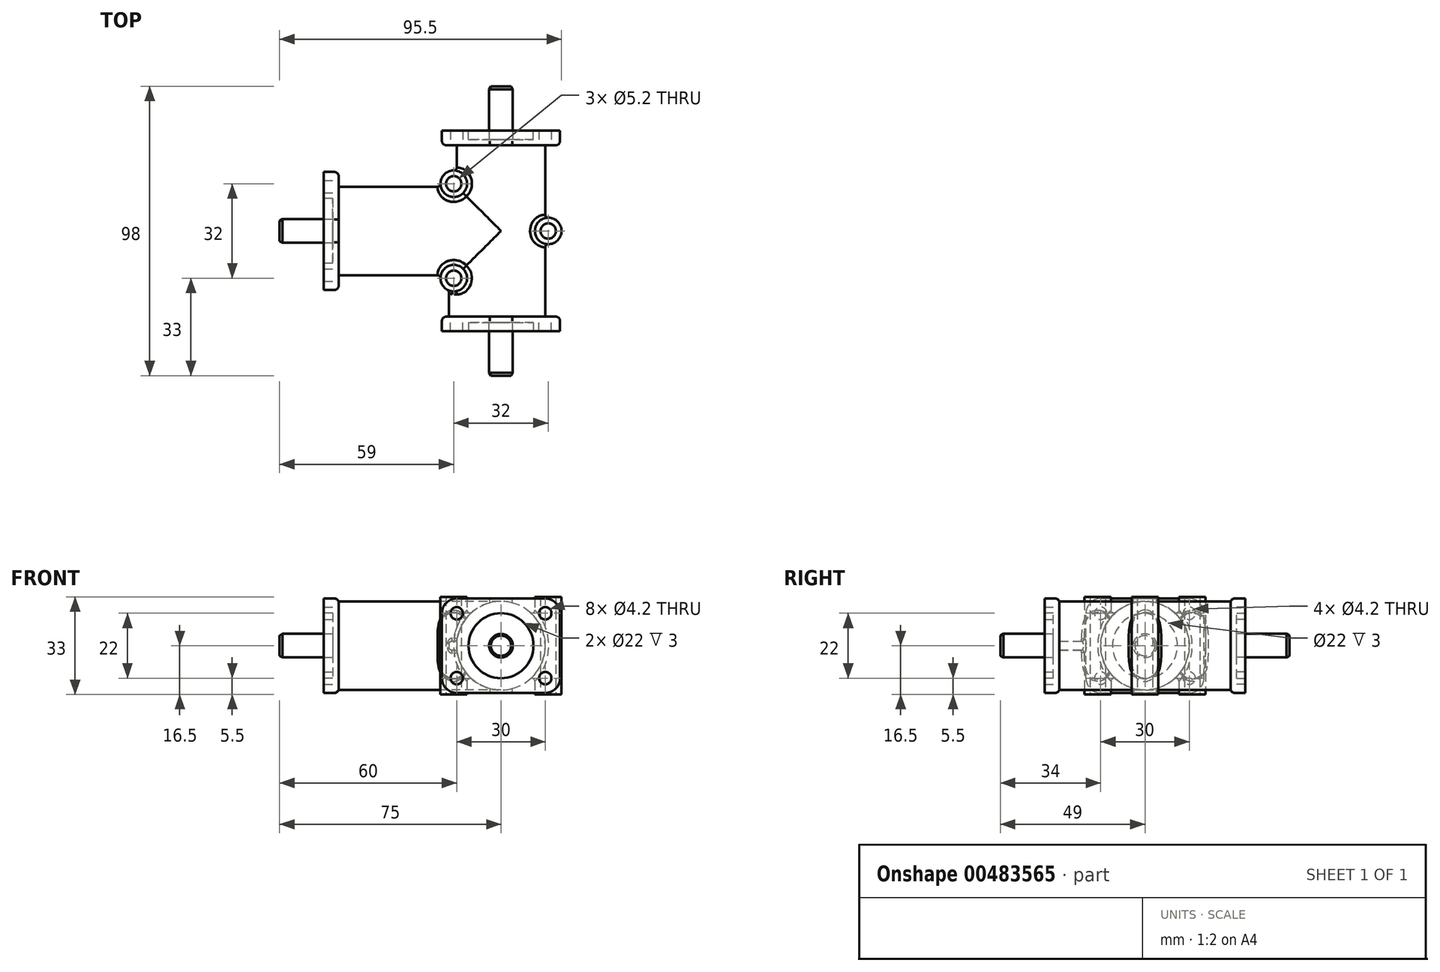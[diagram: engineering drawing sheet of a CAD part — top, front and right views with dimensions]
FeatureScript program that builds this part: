
annotation { "Feature Type Name" : "Feature", "Feature Type Description" : "" }
export const myFeature = defineFeature(function(context is Context, id is Id, definition is map)
    precondition{}
    {
        {
            var Q0;
            Q0=qCreatedBy(makeId("Right.planeOp"),FACE);
            var sketch = newSketch(context, id + "F0", { "sketchPlane" : qUnion([Q0])});
            skCircle(sketch, "E0", {"center": v(0, 0) * mm, "radius": 15 * mm});
            skSolve(sketch);
        }
        {
            var Q0;
            Q0 = qSketchRegion(id + "F0", true);
            extrude(context, id + "F1", {"entities" : qUnion([Q0]), "depth" : 55 * mm});
        }
        {
            var Q0;
            Q0=qCreatedBy(makeId("Front.planeOp"),FACE);
            var sketch = newSketch(context, id + "F2", { "sketchPlane" : qUnion([Q0])});
            skCircle(sketch, "E1", {"center": v(55, 0) * mm, "radius": 15 * mm});
            skSolve(sketch);
        }
        {
            var Q0;
            Q0 = qSketchRegion(id + "F2", true);
            extrude(context, id + "F3", {"entities" : qUnion([Q0]), "operationType" : NewBodyOperationType.ADD, "endBound" : BoundingType.SYMMETRIC, "depth" : 58 * mm});
        }
        {
            var Q0;
            Q0=qCreatedBy(makeId("Top.planeOp"),FACE);
            var sketch = newSketch(context, id + "F4", { "sketchPlane" : qUnion([Q0])});
            skCircle(sketch, "E2", {"center": v(39, 16) * mm, "radius": 4.5 * mm});
            skCircle(sketch, "E3", {"center": v(39, -16) * mm, "radius": 4.5 * mm});
            skLineSegment(sketch, "E4", {"start": v(0, 0) * mm, "end": v(71, 0) * mm, "construction": true});
            skCircle(sketch, "E5", {"center": v(71, 0) * mm, "radius": 4.5 * mm});
            skCircle(sketch, "E6", {"center": v(39, 16) * mm, "radius": 2.75 * mm});
            skCircle(sketch, "E7", {"center": v(39, -16) * mm, "radius": 2.75 * mm});
            skCircle(sketch, "E8", {"center": v(71, 0) * mm, "radius": 2.75 * mm});
            skSolve(sketch);
        }
        {
            var Q0;
            Q0=makeQuery(id+"F4.imprint","IMPRINT",FACE,{"disambiguationData":[TD([[makeQuery(id+"F4.imprint","IMPRINT",EDGE,{"derivedFrom":sQuery(id+"F4.wireOp",EDGE,"E7")}),1.0]])]});
            var Q1;
            Q1=makeQuery(id+"F4.imprint","IMPRINT",FACE,{"disambiguationData":[TD([[makeQuery(id+"F4.imprint","IMPRINT",EDGE,{"derivedFrom":sQuery(id+"F4.wireOp",EDGE,"E6")}),1.0]])]});
            var Q2;
            Q2=makeQuery(id+"F4.imprint","IMPRINT",FACE,{"disambiguationData":[TD([[makeQuery(id+"F4.imprint","IMPRINT",EDGE,{"derivedFrom":sQuery(id+"F4.wireOp",EDGE,"E8")}),1.0]])]});
            var Q3;
            Q3=makeQuery(id+"F4.imprint","IMPRINT",FACE,{"disambiguationData":[TD([[makeQuery(id+"F4.imprint","IMPRINT",EDGE,{"derivedFrom":sQuery(id+"F4.wireOp",EDGE,"E3")}),1.0]])]});
            var Q4;
            Q4=makeQuery(id+"F4.imprint","IMPRINT",FACE,{"disambiguationData":[TD([[makeQuery(id+"F4.imprint","IMPRINT",EDGE,{"derivedFrom":sQuery(id+"F4.wireOp",EDGE,"E5")}),1.0]])]});
            var Q5;
            Q5=makeQuery(id+"F4.imprint","IMPRINT",FACE,{"disambiguationData":[TD([[makeQuery(id+"F4.imprint","IMPRINT",EDGE,{"derivedFrom":sQuery(id+"F4.wireOp",EDGE,"E2")}),1.0]])]});
            extrude(context, id + "F5", {"entities" : qUnion([Q0, Q1, Q2, Q3, Q4, Q5]), "operationType" : NewBodyOperationType.ADD, "endBound" : BoundingType.SYMMETRIC, "depth" : 33 * mm});
        }
        {
            var Q0;
            Q0=qCreatedBy(makeId("Top.planeOp"),FACE);
            var sketch = newSketch(context, id + "F6", { "sketchPlane" : qUnion([Q0])});
            skCircle(sketch, "E9", {"center": v(39, -16) * mm, "radius": 2.6 * mm});
            skCircle(sketch, "E10", {"center": v(39, 16) * mm, "radius": 2.6 * mm});
            skCircle(sketch, "E11", {"center": v(71, 0) * mm, "radius": 2.6 * mm});
            skSolve(sketch);
        }
        {
            var Q0;
            Q0 = qSketchRegion(id + "F6", true);
            extrude(context, id + "F7", {"entities" : qUnion([Q0]), "operationType" : NewBodyOperationType.REMOVE, "endBound" : BoundingType.SYMMETRIC, "depth" : 33 * mm});
        }
        {
            var Q0;
            Q0=makeQuery(id+"F1.opExtrude","CAP_FACE",FACE,{"disambiguationData":[OSD([sQuery(id+"F0.wireOp",EDGE,"E0")])],"isStart":true});
            var sketch = newSketch(context, id + "F8", { "sketchPlane" : qUnion([Q0])});
            skLineSegment(sketch, "E12.bottom", {"start": v(15, -16) * mm, "end": v(-15, -16) * mm});
            skLineSegment(sketch, "E12.top", {"start": v(15, 16) * mm, "end": v(-15, 16) * mm});
            skLineSegment(sketch, "E12.left", {"start": v(20, -11) * mm, "end": v(20, 11) * mm});
            skLineSegment(sketch, "E12.right", {"start": v(-20, -11) * mm, "end": v(-20, 11) * mm});
            skPoint(sketch, "E12.middle", {"position": v(0, 0) * mm});
            skPoint(sketch, "E13.visualSharp", {"position": v(-20, 16) * mm});
            skArc(sketch, "E13.filletArc", {"start": v(-15, 16) * mm, "mid": v(-18.54, 14.54) * mm, "end": v(-20, 11) * mm});
            skPoint(sketch, "E14.visualSharp", {"position": v(20, 16) * mm});
            skArc(sketch, "E14.filletArc", {"start": v(20, 11) * mm, "mid": v(18.54, 14.54) * mm, "end": v(15, 16) * mm});
            skPoint(sketch, "E15.visualSharp", {"position": v(20, -16) * mm});
            skArc(sketch, "E15.filletArc", {"start": v(15, -16) * mm, "mid": v(18.54, -14.54) * mm, "end": v(20, -11) * mm});
            skPoint(sketch, "E16.visualSharp", {"position": v(-20, -16) * mm});
            skArc(sketch, "E16.filletArc", {"start": v(-20, -11) * mm, "mid": v(-18.54, -14.54) * mm, "end": v(-15, -16) * mm});
            skCircle(sketch, "E17", {"center": v(-15, 11) * mm, "radius": 2.1 * mm});
            skCircle(sketch, "E18", {"center": v(15, 11) * mm, "radius": 2.1 * mm});
            skCircle(sketch, "E19", {"center": v(15, -11) * mm, "radius": 2.1 * mm});
            skCircle(sketch, "E20", {"center": v(-15, -11) * mm, "radius": 2.1 * mm});
            skSolve(sketch);
        }
        {
            var Q0;
            Q0 = qSketchRegion(id + "F8", true);
            extrude(context, id + "F9", {"entities" : qUnion([Q0]), "operationType" : NewBodyOperationType.ADD, "depth" : 5 * mm});
        }
        {
            var Q0;
            Q0 = qSketchRegion(id + "F8", true);
            extrude(context, id + "F10", {"entities" : qUnion([Q0]), "operationType" : NewBodyOperationType.ADD, "depth" : 5 * mm});
        }
        {
            var Q0;
            Q0=makeQuery(id+"F3.opExtrude","CAP_FACE",FACE,{"disambiguationData":[OSD([sQuery(id+"F2.wireOp",EDGE,"E1")])],"isStart":false});
            var sketch = newSketch(context, id + "F11", { "sketchPlane" : qUnion([Q0])});
            skLineSegment(sketch, "E21.bottom", {"start": v(70, -16) * mm, "end": v(40, -16) * mm});
            skLineSegment(sketch, "E21.top", {"start": v(70, 16) * mm, "end": v(40, 16) * mm});
            skLineSegment(sketch, "E21.left", {"start": v(75, -11) * mm, "end": v(75, 11) * mm});
            skLineSegment(sketch, "E21.right", {"start": v(35, -11) * mm, "end": v(35, 11) * mm});
            skPoint(sketch, "E21.middle", {"position": v(55, 0) * mm});
            skPoint(sketch, "E22.visualSharp", {"position": v(35, 16) * mm});
            skArc(sketch, "E22.filletArc", {"start": v(40, 16) * mm, "mid": v(36.46, 14.54) * mm, "end": v(35, 11) * mm});
            skPoint(sketch, "E23.visualSharp", {"position": v(75, 16) * mm});
            skArc(sketch, "E23.filletArc", {"start": v(75, 11) * mm, "mid": v(73.54, 14.54) * mm, "end": v(70, 16) * mm});
            skPoint(sketch, "E24.visualSharp", {"position": v(75, -16) * mm});
            skArc(sketch, "E24.filletArc", {"start": v(70, -16) * mm, "mid": v(73.54, -14.54) * mm, "end": v(75, -11) * mm});
            skPoint(sketch, "E25.visualSharp", {"position": v(35, -16) * mm});
            skArc(sketch, "E25.filletArc", {"start": v(35, -11) * mm, "mid": v(36.46, -14.54) * mm, "end": v(40, -16) * mm});
            skCircle(sketch, "E26", {"center": v(40, 11) * mm, "radius": 2.1 * mm});
            skCircle(sketch, "E27", {"center": v(70, 11) * mm, "radius": 2.1 * mm});
            skCircle(sketch, "E28", {"center": v(70, -11) * mm, "radius": 2.1 * mm});
            skCircle(sketch, "E29", {"center": v(40, -11) * mm, "radius": 2.1 * mm});
            skSolve(sketch);
        }
        {
            var Q0;
            Q0 = qSketchRegion(id + "F11", true);
            extrude(context, id + "F12", {"entities" : qUnion([Q0]), "operationType" : NewBodyOperationType.ADD, "depth" : 5 * mm});
        }
        {
            var Q0;
            Q0=makeQuery(id+"F3.opExtrude","CAP_FACE",FACE,{"disambiguationData":[OSD([sQuery(id+"F2.wireOp",EDGE,"E1")])],"isStart":true});
            var sketch = newSketch(context, id + "F13", { "sketchPlane" : qUnion([Q0])});
            skLineSegment(sketch, "E30.bottom", {"start": v(-40, -16) * mm, "end": v(-70, -16) * mm});
            skLineSegment(sketch, "E30.top", {"start": v(-40, 16) * mm, "end": v(-70, 16) * mm});
            skLineSegment(sketch, "E30.left", {"start": v(-35, -11) * mm, "end": v(-35, 11) * mm});
            skLineSegment(sketch, "E30.right", {"start": v(-75, -11) * mm, "end": v(-75, 11) * mm});
            skPoint(sketch, "E30.middle", {"position": v(-55, 0) * mm});
            skPoint(sketch, "E31.visualSharp", {"position": v(-75, 16) * mm});
            skArc(sketch, "E31.filletArc", {"start": v(-70, 16) * mm, "mid": v(-73.54, 14.54) * mm, "end": v(-75, 11) * mm});
            skPoint(sketch, "E32.visualSharp", {"position": v(-35, 16) * mm});
            skArc(sketch, "E32.filletArc", {"start": v(-35, 11) * mm, "mid": v(-36.46, 14.54) * mm, "end": v(-40, 16) * mm});
            skPoint(sketch, "E33.visualSharp", {"position": v(-35, -16) * mm});
            skArc(sketch, "E33.filletArc", {"start": v(-40, -16) * mm, "mid": v(-36.46, -14.54) * mm, "end": v(-35, -11) * mm});
            skPoint(sketch, "E34.visualSharp", {"position": v(-75, -16) * mm});
            skArc(sketch, "E34.filletArc", {"start": v(-75, -11) * mm, "mid": v(-73.54, -14.54) * mm, "end": v(-70, -16) * mm});
            skCircle(sketch, "E35", {"center": v(-70, 11) * mm, "radius": 2.1 * mm});
            skCircle(sketch, "E36", {"center": v(-40, 11) * mm, "radius": 2.1 * mm});
            skCircle(sketch, "E37", {"center": v(-40, -11) * mm, "radius": 2.1 * mm});
            skCircle(sketch, "E38", {"center": v(-70, -11) * mm, "radius": 2.1 * mm});
            skSolve(sketch);
        }
        {
            var Q0;
            Q0 = qSketchRegion(id + "F13", true);
            extrude(context, id + "F14", {"entities" : qUnion([Q0]), "operationType" : NewBodyOperationType.ADD, "depth" : 5 * mm});
        }
        {
            var Q0;
            Q0=qCreatedBy(makeId("Top.planeOp"),FACE);
            var sketch = newSketch(context, id + "F15", { "sketchPlane" : qUnion([Q0])});
            skLineSegment(sketch, "E39.bottom", {"start": v(42.34, -29) * mm, "end": v(37.34, -29) * mm});
            skLineSegment(sketch, "E39.top", {"start": v(42.34, -19) * mm, "end": v(37.34, -19) * mm});
            skLineSegment(sketch, "E39.left", {"start": v(42.34, -29) * mm, "end": v(42.34, -19) * mm});
            skLineSegment(sketch, "E39.right", {"start": v(37.34, -29) * mm, "end": v(37.34, -19) * mm});
            skPoint(sketch, "E39.middle", {"position": v(39.84, -24) * mm});
            skSolve(sketch);
        }
        {
            var Q0;
            Q0 = qSketchRegion(id + "F15", true);
            extrude(context, id + "F16", {"entities" : qUnion([Q0]), "operationType" : NewBodyOperationType.ADD, "endBound" : BoundingType.SYMMETRIC, "depth" : 3 * mm});
        }
        {
            var Q0;
            Q0=makeQuery(id+"F12.opExtrude","CAP_FACE",FACE,{"disambiguationData":[OSD([sQuery(id+"F11.wireOp",EDGE,"E21.bottom"),sQuery(id+"F11.wireOp",EDGE,"E21.top"),sQuery(id+"F11.wireOp",EDGE,"E21.left"),sQuery(id+"F11.wireOp",EDGE,"E21.right"),sQuery(id+"F11.wireOp",EDGE,"E22.filletArc"),sQuery(id+"F11.wireOp",EDGE,"E23.filletArc"),sQuery(id+"F11.wireOp",EDGE,"E24.filletArc"),sQuery(id+"F11.wireOp",EDGE,"E25.filletArc"),sQuery(id+"F11.wireOp",EDGE,"E26"),sQuery(id+"F11.wireOp",EDGE,"E27"),sQuery(id+"F11.wireOp",EDGE,"E28"),sQuery(id+"F11.wireOp",EDGE,"E29")])],"isStart":false});
            var sketch = newSketch(context, id + "F17", { "sketchPlane" : qUnion([Q0])});
            skCircle(sketch, "E40", {"center": v(55, 0) * mm, "radius": 11 * mm});
            skPoint(sketch, "E40.centerSnap0", {"position": v(55, 16) * mm});
            skSolve(sketch);
        }
        {
            var Q0;
            Q0 = qSketchRegion(id + "F17", true);
            extrude(context, id + "F18", {"entities" : qUnion([Q0]), "oppositeDirection" : true, "depth" : 3 * mm});
        }
        {
            var Q0;
            Q0=makeQuery(id+"F18.opExtrude","SWEPT_BODY",BODY,{"disambiguationData":[OSD([sQuery(id+"F17.wireOp",EDGE,"E40")])]});
            var Q1;
            Q1=qCreatedBy(makeId("Front.planeOp"),FACE);
            mirror(context, id + "F19", {"entities" : qUnion([Q0]), "mirrorPlane" : qUnion([Q1])});
        }
        {
            var Q0;
            Q0=makeQuery(id+"F18.opExtrude","SWEPT_BODY",BODY,{"disambiguationData":[OSD([sQuery(id+"F17.wireOp",EDGE,"E40")])]});
            var Q1;
            Q1=makeQuery(id+"F19.opPattern","COPY",BODY,{"derivedFrom":makeQuery(id+"F18.opExtrude","SWEPT_BODY",BODY,{"disambiguationData":[OSD([sQuery(id+"F17.wireOp",EDGE,"E40")])]}),"instanceName":"1"});
            var Q2;
            Q2=makeQuery(id+"F1.opExtrude","SWEPT_BODY",BODY,{"disambiguationData":[OSD([sQuery(id+"F0.wireOp",EDGE,"E0")])]});
            booleanBodies(context, id + "F20", {"operationType" : BooleanOperationType.SUBTRACTION, "tools" : qUnion([Q0, Q1]), "targets" : qUnion([Q2])});
        }
        {
            var Q0;
            Q0=makeQuery(id+"F9.opExtrude","CAP_FACE",FACE,{"disambiguationData":[OSD([sQuery(id+"F8.wireOp",EDGE,"E12.bottom"),sQuery(id+"F8.wireOp",EDGE,"E12.top"),sQuery(id+"F8.wireOp",EDGE,"E12.left"),sQuery(id+"F8.wireOp",EDGE,"E12.right"),sQuery(id+"F8.wireOp",EDGE,"E13.filletArc"),sQuery(id+"F8.wireOp",EDGE,"E14.filletArc"),sQuery(id+"F8.wireOp",EDGE,"E15.filletArc"),sQuery(id+"F8.wireOp",EDGE,"E16.filletArc"),sQuery(id+"F8.wireOp",EDGE,"E17"),sQuery(id+"F8.wireOp",EDGE,"E18"),sQuery(id+"F8.wireOp",EDGE,"E19"),sQuery(id+"F8.wireOp",EDGE,"E20")])],"isStart":false});
            var sketch = newSketch(context, id + "F21", { "sketchPlane" : qUnion([Q0])});
            skCircle(sketch, "E41", {"center": v(0, 0) * mm, "radius": 11 * mm});
            skSolve(sketch);
        }
        {
            var Q0;
            Q0 = qSketchRegion(id + "F21", true);
            extrude(context, id + "F22", {"entities" : qUnion([Q0]), "operationType" : NewBodyOperationType.REMOVE, "oppositeDirection" : true, "depth" : 3 * mm});
        }
        {
            var Q0;
            Q0=makeQuery(id+"F20.opBoolean","COPY",FACE,{"derivedFrom":makeQuery(id+"F18.opExtrude","CAP_FACE",FACE,{"disambiguationData":[OSD([sQuery(id+"F17.wireOp",EDGE,"E40")])],"isStart":false})});
            var sketch = newSketch(context, id + "F23", { "sketchPlane" : qUnion([Q0])});
            skCircle(sketch, "E42", {"center": v(55, 0) * mm, "radius": 4 * mm});
            skSolve(sketch);
        }
        {
            var Q0;
            Q0 = qSketchRegion(id + "F23", true);
            extrude(context, id + "F24", {"entities" : qUnion([Q0]), "depth" : 18 * mm});
        }
        {
            var Q0;
            Q0=makeQuery(id+"F24.opExtrude","CAP_EDGE",EDGE,{"disambiguationData":[OSD([sQuery(id+"F23.wireOp",EDGE,"E42")])],"isStart":false});
            chamfer(context, id + "F25", {"entities" : qUnion([Q0]), "chamferType" : ChamferType.OFFSET_ANGLE, "width" : 1 * mm, "oppositeDirection" : true, "angle" : 30 * degree, "tangentPropagation" : true});
        }
        {
            var Q0;
            Q0=makeQuery(id+"F24.opExtrude","SWEPT_BODY",BODY,{"disambiguationData":[OSD([sQuery(id+"F23.wireOp",EDGE,"E42")])]});
            var Q1;
            Q1=qCreatedBy(makeId("Front.planeOp"),FACE);
            mirror(context, id + "F26", {"operationType" : NewBodyOperationType.ADD, "entities" : qUnion([Q0]), "mirrorPlane" : qUnion([Q1])});
        }
        {
            var Q0;
            Q0=makeQuery(id+"F22.boolean.opBoolean","COPY",FACE,{"derivedFrom":makeQuery(id+"F22.opExtrude","CAP_FACE",FACE,{"disambiguationData":[OSD([sQuery(id+"F21.wireOp",EDGE,"E41")])],"isStart":false})});
            var sketch = newSketch(context, id + "F27", { "sketchPlane" : qUnion([Q0])});
            skCircle(sketch, "E43", {"center": v(0, 0) * mm, "radius": 4 * mm});
            skSolve(sketch);
        }
        {
            var Q0;
            Q0 = qSketchRegion(id + "F27", true);
            extrude(context, id + "F28", {"entities" : qUnion([Q0]), "operationType" : NewBodyOperationType.ADD, "depth" : 18 * mm});
        }
        {
            var Q0;
            Q0=makeQuery(id+"F28.opExtrude","CAP_EDGE",EDGE,{"disambiguationData":[OSD([sQuery(id+"F27.wireOp",EDGE,"E43")])],"isStart":false});
            chamfer(context, id + "F29", {"entities" : qUnion([Q0]), "chamferType" : ChamferType.OFFSET_ANGLE, "width" : 1 * mm, "oppositeDirection" : true, "angle" : 30 * degree, "tangentPropagation" : true});
        }
        {
            var Q0;
            Q0=makeQuery(id+"F5.boolean.opBoolean","INTERSECT",EDGE,{"derivedFrom":[makeQuery(id+"F1.opExtrude","SWEPT_FACE",FACE,{"disambiguationData":[OSD([sQuery(id+"F0.wireOp",EDGE,"E0")])]}),makeQuery(id+"F5.opExtrude","SWEPT_FACE",FACE,{"disambiguationData":[OSD([sQuery(id+"F4.wireOp",EDGE,"E2")])]})]});
            var Q1;
            Q1=makeQuery(id+"F5.boolean.opBoolean","INTERSECT",EDGE,{"derivedFrom":[makeQuery(id+"F3.opExtrude","SWEPT_FACE",FACE,{"disambiguationData":[OSD([sQuery(id+"F2.wireOp",EDGE,"E1")])]}),makeQuery(id+"F5.opExtrude","SWEPT_FACE",FACE,{"disambiguationData":[OSD([sQuery(id+"F4.wireOp",EDGE,"E2")])]})]});
            var Q2;
            Q2=makeQuery(id+"F5.boolean.opBoolean","INTERSECT",EDGE,{"derivedFrom":[makeQuery(id+"F1.opExtrude","SWEPT_FACE",FACE,{"disambiguationData":[OSD([sQuery(id+"F0.wireOp",EDGE,"E0")])]}),makeQuery(id+"F5.opExtrude","SWEPT_FACE",FACE,{"disambiguationData":[OSD([sQuery(id+"F4.wireOp",EDGE,"E3")])]})]});
            var Q3;
            Q3=makeQuery(id+"F5.boolean.opBoolean","INTERSECT",EDGE,{"derivedFrom":[makeQuery(id+"F3.opExtrude","SWEPT_FACE",FACE,{"disambiguationData":[OSD([sQuery(id+"F2.wireOp",EDGE,"E1")])]}),makeQuery(id+"F5.opExtrude","SWEPT_FACE",FACE,{"disambiguationData":[OSD([sQuery(id+"F4.wireOp",EDGE,"E3")])]})]});
            var Q4;
            Q4=makeQuery(id+"F5.boolean.opBoolean","INTERSECT",EDGE,{"derivedFrom":[makeQuery(id+"F3.opExtrude","SWEPT_FACE",FACE,{"disambiguationData":[OSD([sQuery(id+"F2.wireOp",EDGE,"E1")])]}),makeQuery(id+"F5.opExtrude","SWEPT_FACE",FACE,{"disambiguationData":[OSD([sQuery(id+"F4.wireOp",EDGE,"E5")])]})]});
            var Q5;
            Q5=makeQuery(id+"F1.opExtrude","CAP_EDGE",EDGE,{"disambiguationData":[OSD([sQuery(id+"F0.wireOp",EDGE,"E0")])],"isStart":true});
            var Q6;
            Q6=makeQuery(id+"F3.opExtrude","CAP_EDGE",EDGE,{"disambiguationData":[OSD([sQuery(id+"F2.wireOp",EDGE,"E1")])],"isStart":false});
            var Q7;
            Q7=makeQuery(id+"F3.opExtrude","CAP_EDGE",EDGE,{"disambiguationData":[OSD([sQuery(id+"F2.wireOp",EDGE,"E1")])],"isStart":true});
            var Q8;
            Q8=makeQuery(id+"F16.boolean.opBoolean","INTERSECT",EDGE,{"derivedFrom":[makeQuery(id+"F5.opExtrude","SWEPT_FACE",FACE,{"disambiguationData":[OSD([sQuery(id+"F4.wireOp",EDGE,"E3")])]}),makeQuery(id+"F16.opExtrude","CAP_FACE",FACE,{"disambiguationData":[OSD([sQuery(id+"F15.wireOp",EDGE,"E39.bottom"),sQuery(id+"F15.wireOp",EDGE,"E39.top"),sQuery(id+"F15.wireOp",EDGE,"E39.left"),sQuery(id+"F15.wireOp",EDGE,"E39.right")])],"isStart":false})]});
            var Q9;
            Q9=makeQuery(id+"F16.boolean.opBoolean","INTERSECT",EDGE,{"derivedFrom":[makeQuery(id+"F5.opExtrude","SWEPT_FACE",FACE,{"disambiguationData":[OSD([sQuery(id+"F4.wireOp",EDGE,"E3")])]}),makeQuery(id+"F16.opExtrude","SWEPT_FACE",FACE,{"disambiguationData":[OSD([sQuery(id+"F15.wireOp",EDGE,"E39.right")])]})]});
            var Q10;
            Q10=makeQuery(id+"F16.boolean.opBoolean","INTERSECT",EDGE,{"derivedFrom":[makeQuery(id+"F5.opExtrude","SWEPT_FACE",FACE,{"disambiguationData":[OSD([sQuery(id+"F4.wireOp",EDGE,"E3")])]}),makeQuery(id+"F16.opExtrude","CAP_FACE",FACE,{"disambiguationData":[OSD([sQuery(id+"F15.wireOp",EDGE,"E39.bottom"),sQuery(id+"F15.wireOp",EDGE,"E39.top"),sQuery(id+"F15.wireOp",EDGE,"E39.left"),sQuery(id+"F15.wireOp",EDGE,"E39.right")])],"isStart":true})]});
            var Q11;
            Q11=makeQuery(id+"F16.opExtrude","CAP_EDGE",EDGE,{"disambiguationData":[OSD([sQuery(id+"F15.wireOp",EDGE,"E39.bottom")])],"isStart":true});
            var Q12;
            Q12=makeQuery(id+"F16.opExtrude","SWEPT_EDGE",EDGE,{"disambiguationData":[OSD([sQuery(id+"F15.wireOp",EDGE,"E39.bottom"),sQuery(id+"F15.wireOp",EDGE,"E39.right")])]});
            var Q13;
            Q13=makeQuery(id+"F16.opExtrude","CAP_EDGE",EDGE,{"disambiguationData":[OSD([sQuery(id+"F15.wireOp",EDGE,"E39.bottom")])],"isStart":false});
            var Q14;
            Q14=makeQuery(id+"F16.boolean.opBoolean","INTERSECT",EDGE,{"derivedFrom":[makeQuery(id+"F3.opExtrude","SWEPT_FACE",FACE,{"disambiguationData":[OSD([sQuery(id+"F2.wireOp",EDGE,"E1")])]}),makeQuery(id+"F16.opExtrude","CAP_FACE",FACE,{"disambiguationData":[OSD([sQuery(id+"F15.wireOp",EDGE,"E39.bottom"),sQuery(id+"F15.wireOp",EDGE,"E39.top"),sQuery(id+"F15.wireOp",EDGE,"E39.left"),sQuery(id+"F15.wireOp",EDGE,"E39.right")])],"isStart":false})]});
            var Q15;
            Q15=makeQuery(id+"F16.boolean.opBoolean","INTERSECT",EDGE,{"derivedFrom":[makeQuery(id+"F3.opExtrude","SWEPT_FACE",FACE,{"disambiguationData":[OSD([sQuery(id+"F2.wireOp",EDGE,"E1")])]}),makeQuery(id+"F16.opExtrude","CAP_FACE",FACE,{"disambiguationData":[OSD([sQuery(id+"F15.wireOp",EDGE,"E39.bottom"),sQuery(id+"F15.wireOp",EDGE,"E39.top"),sQuery(id+"F15.wireOp",EDGE,"E39.left"),sQuery(id+"F15.wireOp",EDGE,"E39.right")])],"isStart":true})]});
            var Q16;
            Q16=makeQuery(id+"F16.opExtrude","CAP_EDGE",EDGE,{"disambiguationData":[OSD([sQuery(id+"F15.wireOp",EDGE,"E39.right")])],"isStart":true});
            var Q17;
            Q17=makeQuery(id+"F16.opExtrude","CAP_EDGE",EDGE,{"disambiguationData":[OSD([sQuery(id+"F15.wireOp",EDGE,"E39.right")])],"isStart":false});
            fillet(context, id + "F30", {"entities" : qUnion([Q0, Q1, Q2, Q3, Q4, Q5, Q6, Q7, Q8, Q9, Q10, Q11, Q12, Q13, Q14, Q15, Q16, Q17]), "radius" : 1 * mm, "tangentPropagation" : true, "allowEdgeOverflow" : false});
        }
        {
            var Q0;
            Q0=makeQuery(id+"F9.opExtrude","CAP_EDGE",EDGE,{"disambiguationData":[OSD([sQuery(id+"F8.wireOp",EDGE,"E12.top")])],"isStart":true});
            var Q1;
            Q1=makeQuery(id+"F12.opExtrude","CAP_EDGE",EDGE,{"disambiguationData":[OSD([sQuery(id+"F11.wireOp",EDGE,"E21.top")])],"isStart":true});
            var Q2;
            Q2=makeQuery(id+"F14.opExtrude","CAP_EDGE",EDGE,{"disambiguationData":[OSD([sQuery(id+"F13.wireOp",EDGE,"E30.top")])],"isStart":true});
            fillet(context, id + "F31", {"entities" : qUnion([Q0, Q1, Q2]), "radius" : 1.5 * mm, "tangentPropagation" : true, "allowEdgeOverflow" : false});
        }
    });
